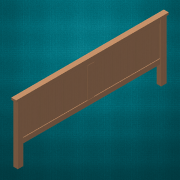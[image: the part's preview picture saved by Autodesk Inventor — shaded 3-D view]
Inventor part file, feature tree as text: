
AUTODESK INVENTOR PART (.ipt)
format: ipt  version: 2017 (Build 210142000, 142)  size: 189,952 bytes
history: native  units: in
note: dims shown in document units (in); Inventor stores cm internally (conversion verified against a paired STEP export)
features: extrude x4, sketch x4, chamfer x1
ambient origin geometry x8: Origin, YZ Plane, XZ Plane, XY Plane, X Axis, Y Axis, Z Axis, Center Point
bodies: Solid1 (feature_tree), Solid2 (feature_tree)
feature tree (9):
  extrude  "Extrusion1"  Depth=2.3125in
  extrude  "Extrusion2"  Depth=25.0in TaperAngle=0.0deg
  extrude  "Extrusion3"  Depth=0.875in
  extrude  "Extrusion4"  Depth=2.125in
  chamfer  "Chamfer1"  Distance=0.875in
  sketch  "Sketch1"  dims[d0=1.875in d1=2.3125in]
  sketch  "Sketch2"  dims[d2=63.375in d3=25.0in d4=0.0in]
  sketch  "Sketch3"  dims[d5=2.125in d6=0.875in]
  sketch  "Sketch4"  dims[d7=65.0in d8=0.0in d9=2.125in d10=0.875in d11=7.875in d12=65.75in d13=0.0in d14=0.4375in d15=0.875in d16=2.875in d17=65.75in d18=0.0in d19=0.0625in d20=0.125in d21=45.0deg]
